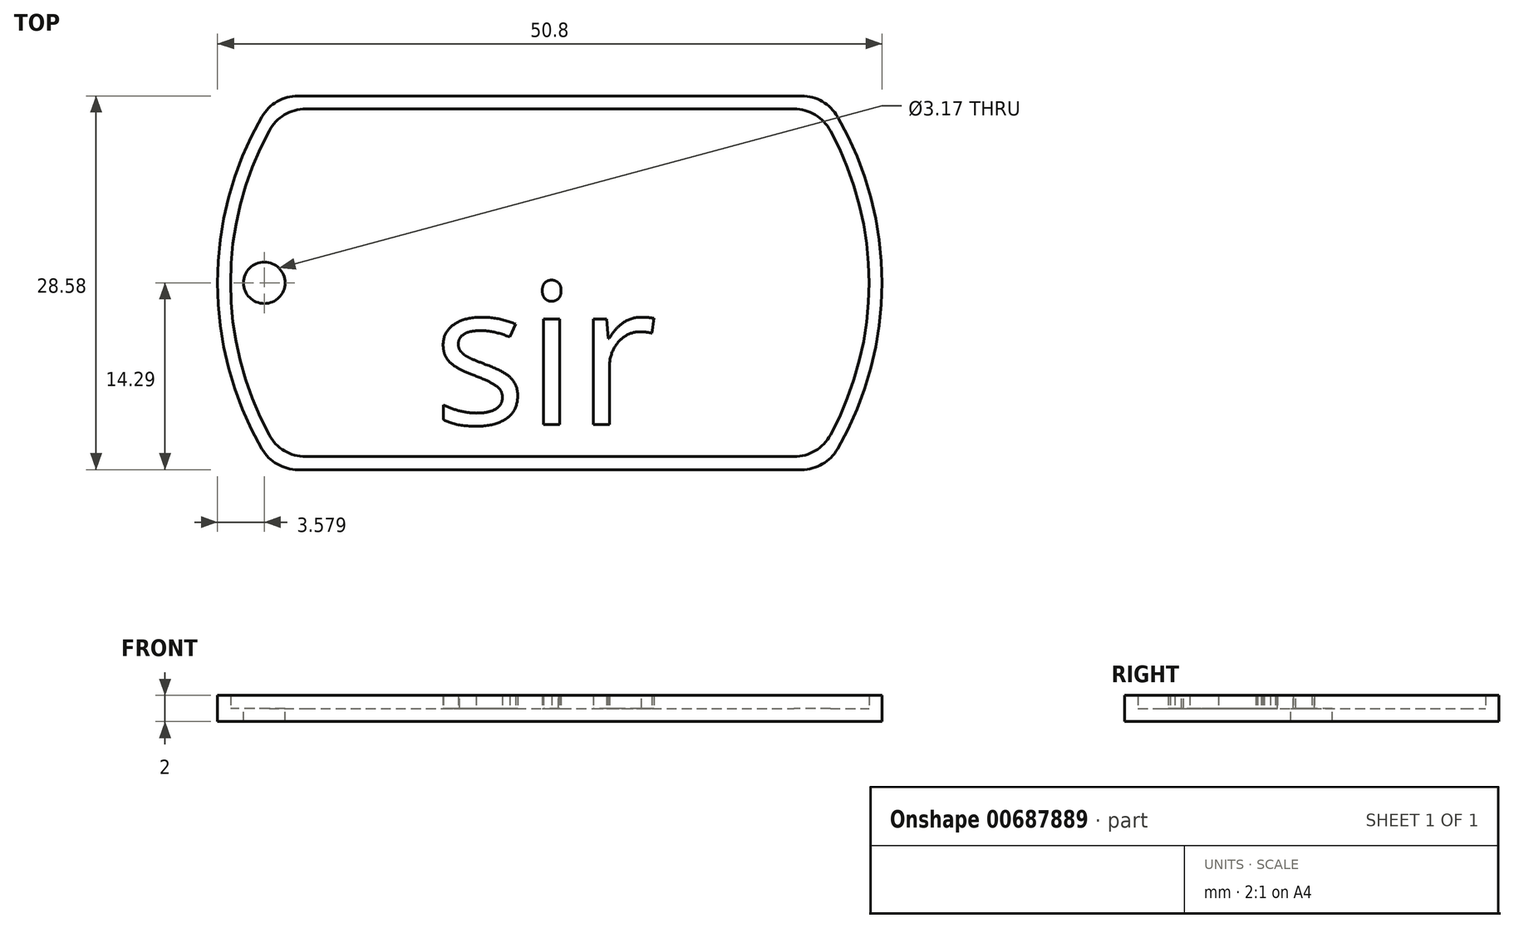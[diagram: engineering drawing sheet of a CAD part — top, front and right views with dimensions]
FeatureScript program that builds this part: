
annotation { "Feature Type Name" : "Feature", "Feature Type Description" : "" }
export const myFeature = defineFeature(function(context is Context, id is Id, definition is map)
    precondition{}
    {
        {
            var Q0;
            Q0=qCreatedBy(makeId("Top.planeOp"),FACE);
            var sketch = newSketch(context, id + "F0", { "sketchPlane" : qUnion([Q0])});
            skArc(sketch, "E0", {"start": v(-22, 12.7) * mm, "mid": v(-25.4, 0) * mm, "end": v(-22, -12.7) * mm});
            skLineSegment(sketch, "E1.top", {"start": v(-19.25, -14.29) * mm, "end": v(19.25, -14.29) * mm});
            skArc(sketch, "E2.trimOffspring", {"start": v(22, -12.7) * mm, "mid": v(25.4, 0) * mm, "end": v(22, 12.7) * mm});
            skLineSegment(sketch, "E3", {"start": v(-19.25, 14.29) * mm, "end": v(19.25, 14.29) * mm});
            skPoint(sketch, "E4.visualSharp", {"position": v(-21, 14.29) * mm});
            skArc(sketch, "E4.filletArc", {"start": v(-19.25, 14.29) * mm, "mid": v(-20.83, 13.86) * mm, "end": v(-22, 12.7) * mm});
            skPoint(sketch, "E5.visualSharp", {"position": v(21, 14.29) * mm});
            skArc(sketch, "E5.filletArc", {"start": v(22, 12.7) * mm, "mid": v(20.83, 13.86) * mm, "end": v(19.25, 14.29) * mm});
            skPoint(sketch, "E6.visualSharp", {"position": v(21, -14.29) * mm});
            skArc(sketch, "E6.filletArc", {"start": v(19.25, -14.29) * mm, "mid": v(20.83, -13.86) * mm, "end": v(22, -12.7) * mm});
            skPoint(sketch, "E7.visualSharp", {"position": v(-21, -14.29) * mm});
            skArc(sketch, "E7.filletArc", {"start": v(-22, -12.7) * mm, "mid": v(-20.83, -13.86) * mm, "end": v(-19.25, -14.29) * mm});
            skSolve(sketch);
        }
        {
            var Q0;
            Q0=makeQuery(id+"F0.imprint","IMPRINT",FACE,{"disambiguationData":[TD([[makeQuery(id+"F0.imprint","IMPRINT",EDGE,{"derivedFrom":sQuery(id+"F0.wireOp",EDGE,"E0")}),1.0]])]});
            extrude(context, id + "F1", {"entities" : qUnion([Q0]), "depth" : 1 * mm, "offsetDistance" : 25.4 * mm});
        }
        {
            var Q0;
            Q0=makeQuery(id+"F1.opExtrude","CAP_FACE",FACE,{"disambiguationData":[OSD([sQuery(id+"F0.wireOp",EDGE,"E0"),sQuery(id+"F0.wireOp",EDGE,"E1.top"),sQuery(id+"F0.wireOp",EDGE,"E2.trimOffspring"),sQuery(id+"F0.wireOp",EDGE,"E3"),sQuery(id+"F0.wireOp",EDGE,"E4.filletArc"),sQuery(id+"F0.wireOp",EDGE,"E5.filletArc"),sQuery(id+"F0.wireOp",EDGE,"E6.filletArc"),sQuery(id+"F0.wireOp",EDGE,"E7.filletArc")])],"isStart":false});
            var sketch = newSketch(context, id + "F2", { "sketchPlane" : qUnion([Q0])});
            skLineSegment(sketch, "E8.0", {"start": v(-18.66, 13.29) * mm, "end": v(18.66, 13.29) * mm});
            skArc(sketch, "E8.1", {"start": v(-21.45, 11.63) * mm, "mid": v(-24.4, 0) * mm, "end": v(-21.45, -11.63) * mm});
            skLineSegment(sketch, "E8.2", {"start": v(-18.66, -13.29) * mm, "end": v(18.66, -13.29) * mm});
            skArc(sketch, "E8.3", {"start": v(21.45, -11.63) * mm, "mid": v(24.4, 0) * mm, "end": v(21.45, 11.63) * mm});
            skPoint(sketch, "E9.visualSharp", {"position": v(-20.46, 13.29) * mm});
            skArc(sketch, "E9.filletArc", {"start": v(-18.66, 13.29) * mm, "mid": v(-20.29, 12.84) * mm, "end": v(-21.45, 11.63) * mm});
            skPoint(sketch, "E10.visualSharp", {"position": v(20.46, 13.29) * mm});
            skArc(sketch, "E10.filletArc", {"start": v(21.45, 11.63) * mm, "mid": v(20.29, 12.84) * mm, "end": v(18.66, 13.29) * mm});
            skPoint(sketch, "E11.visualSharp", {"position": v(20.46, -13.29) * mm});
            skArc(sketch, "E11.filletArc", {"start": v(18.66, -13.29) * mm, "mid": v(20.29, -12.84) * mm, "end": v(21.45, -11.63) * mm});
            skPoint(sketch, "E12.visualSharp", {"position": v(-20.46, -13.29) * mm});
            skArc(sketch, "E12.filletArc", {"start": v(-21.45, -11.63) * mm, "mid": v(-20.29, -12.84) * mm, "end": v(-18.66, -13.29) * mm});
            skLineSegment(sketch, "E13.0", {"start": v(-19.25, 14.29) * mm, "end": v(19.25, 14.29) * mm});
            skArc(sketch, "E13.1", {"start": v(-22, 12.7) * mm, "mid": v(-25.4, 0) * mm, "end": v(-22, -12.7) * mm});
            skLineSegment(sketch, "E13.2", {"start": v(-19.25, -14.29) * mm, "end": v(19.25, -14.29) * mm});
            skArc(sketch, "E13.3", {"start": v(22, -12.7) * mm, "mid": v(25.4, 0) * mm, "end": v(22, 12.7) * mm});
            skPoint(sketch, "E14.visualSharp", {"position": v(-21, -14.29) * mm});
            skArc(sketch, "E14.filletArc", {"start": v(-22, -12.7) * mm, "mid": v(-20.83, -13.86) * mm, "end": v(-19.25, -14.29) * mm});
            skPoint(sketch, "E15.visualSharp", {"position": v(21, -14.29) * mm});
            skArc(sketch, "E15.filletArc", {"start": v(19.25, -14.29) * mm, "mid": v(20.83, -13.86) * mm, "end": v(22, -12.7) * mm});
            skPoint(sketch, "E16.visualSharp", {"position": v(21, 14.29) * mm});
            skArc(sketch, "E16.filletArc", {"start": v(22, 12.7) * mm, "mid": v(20.83, 13.86) * mm, "end": v(19.25, 14.29) * mm});
            skPoint(sketch, "E17.visualSharp", {"position": v(-21, 14.29) * mm});
            skArc(sketch, "E17.filletArc", {"start": v(-19.25, 14.29) * mm, "mid": v(-20.83, 13.86) * mm, "end": v(-22, 12.7) * mm});
            skSolve(sketch);
        }
        {
            var Q0;
            Q0=makeQuery(id+"F2.imprint","IMPRINT",FACE,{"disambiguationData":[TD([[makeQuery(id+"F2.imprint","IMPRINT",EDGE,{"derivedFrom":sQuery(id+"F2.wireOp",EDGE,"E8.0")}),1.0]])]});
            extrude(context, id + "F3", {"entities" : qUnion([Q0]), "operationType" : NewBodyOperationType.ADD, "depth" : 1 * mm, "offsetDistance" : 25.4 * mm});
        }
        {
            var Q0;
            Q0=makeQuery(id+"F1.opExtrude","CAP_FACE",FACE,{"disambiguationData":[OSD([sQuery(id+"F0.wireOp",EDGE,"E0"),sQuery(id+"F0.wireOp",EDGE,"E1.top"),sQuery(id+"F0.wireOp",EDGE,"E2.trimOffspring"),sQuery(id+"F0.wireOp",EDGE,"E3"),sQuery(id+"F0.wireOp",EDGE,"E4.filletArc"),sQuery(id+"F0.wireOp",EDGE,"E5.filletArc"),sQuery(id+"F0.wireOp",EDGE,"E6.filletArc"),sQuery(id+"F0.wireOp",EDGE,"E7.filletArc")])],"isStart":false});
            var sketch = newSketch(context, id + "F4", { "sketchPlane" : qUnion([Q0])});
            skCircle(sketch, "E18", {"center": v(-21.82, 0) * mm, "radius": 1.59 * mm});
            skSolve(sketch);
        }
        {
            var Q0;
            Q0=makeQuery(id+"F4.imprint","IMPRINT",FACE,{"disambiguationData":[TD([[makeQuery(id+"F4.imprint","IMPRINT",EDGE,{"derivedFrom":sQuery(id+"F4.wireOp",EDGE,"E18")}),1.0]])]});
            extrude(context, id + "F5", {"entities" : qUnion([Q0]), "operationType" : NewBodyOperationType.REMOVE, "oppositeDirection" : true, "depth" : 1 * mm, "offsetDistance" : 25.4 * mm});
        }
        {
            var Q0;
            Q0=makeQuery(id+"F2.imprint","IMPRINT",FACE,{"disambiguationData":[TD([[makeQuery(id+"F2.imprint","IMPRINT",EDGE,{"derivedFrom":sQuery(id+"F2.wireOp",EDGE,"E8.0")}),-1.0]])]});
            var sketch = newSketch(context, id + "F6", { "sketchPlane" : qUnion([Q0])});
            skText(sketch, "E19", { "text": "sir", "fontName": "OpenSans-Regular.ttf"});
            const initialGuessF6  = {"E19": [-0.00893, -0.01082, 1, 0, 0.01082]};
            skSetInitialGuess(sketch, initialGuessF6);
            skSolve(sketch);
        }
        {
            var Q0;
            Q0 = qSketchRegion(id + "F6", true);
            extrude(context, id + "F7", {"entities" : qUnion([Q0]), "operationType" : NewBodyOperationType.ADD, "depth" : 1 * mm, "offsetDistance" : 25.4 * mm});
        }
    });
